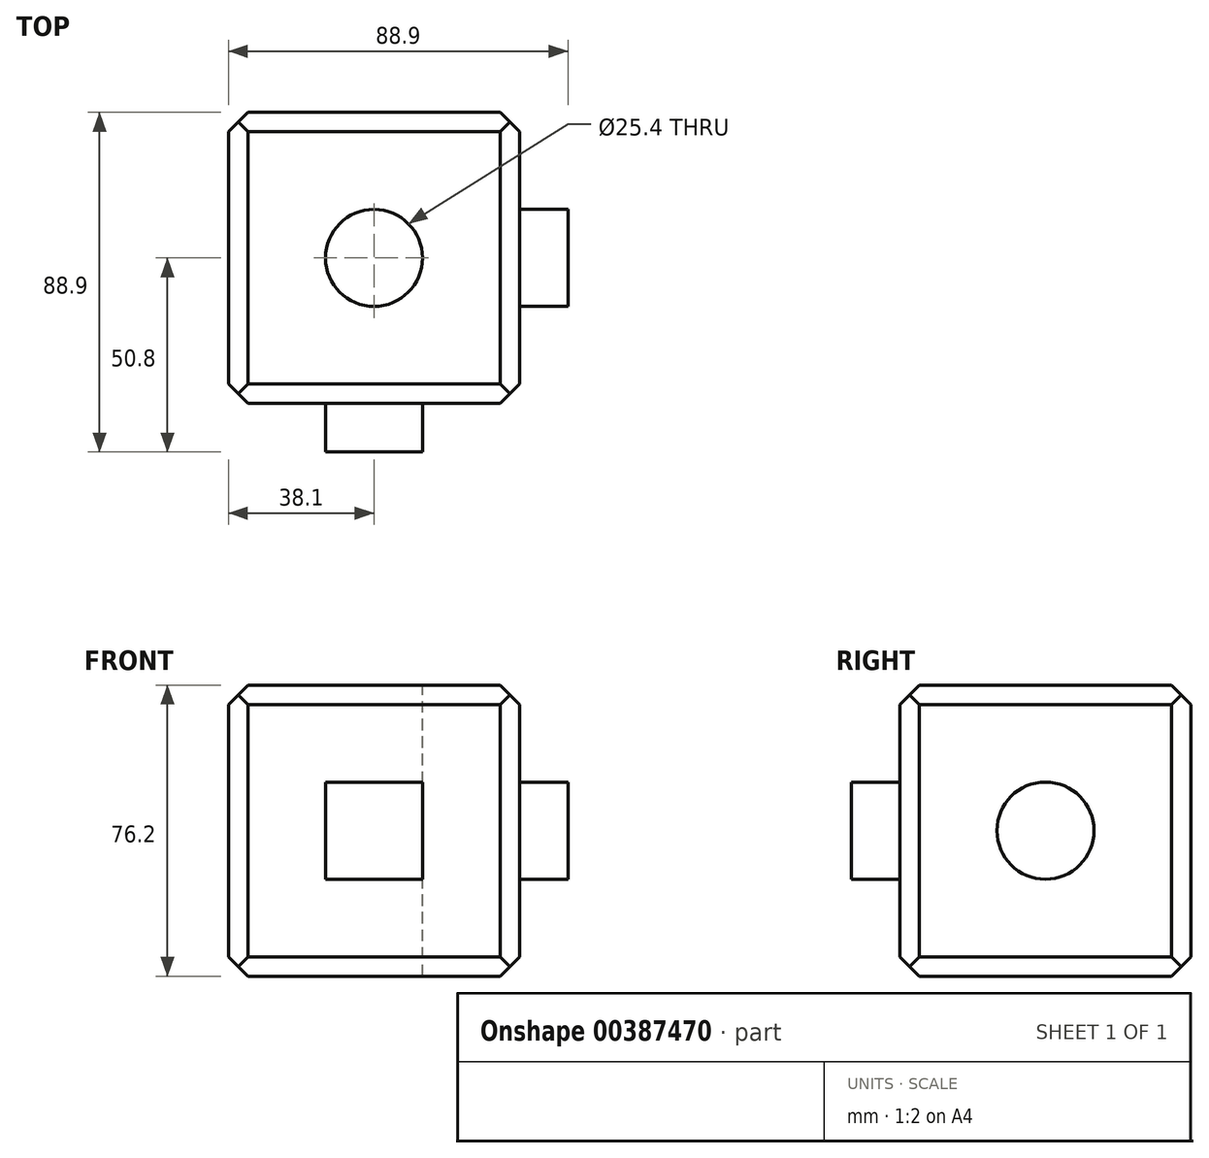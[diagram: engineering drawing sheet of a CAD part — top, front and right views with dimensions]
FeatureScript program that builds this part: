
annotation { "Feature Type Name" : "Feature", "Feature Type Description" : "" }
export const myFeature = defineFeature(function(context is Context, id is Id, definition is map)
    precondition{}
    {
        {
            var Q0;
            Q0=qCreatedBy(makeId("Front.planeOp"),FACE);
            var sketch = newSketch(context, id + "F0", { "sketchPlane" : qUnion([Q0])});
            skLineSegment(sketch, "E0.bottom", {"start": v(0, 0) * mm, "end": v(-76.2, 0) * mm});
            skLineSegment(sketch, "E0.top", {"start": v(0, 76.2) * mm, "end": v(-76.2, 76.2) * mm});
            skLineSegment(sketch, "E0.left", {"start": v(0, 0) * mm, "end": v(0, 76.2) * mm});
            skLineSegment(sketch, "E0.right", {"start": v(-76.2, 0) * mm, "end": v(-76.2, 76.2) * mm});
            skSolve(sketch);
        }
        {
            var Q0;
            Q0=makeQuery(id+"F0.imprint","IMPRINT",FACE,{"disambiguationData":[TD([[makeQuery(id+"F0.imprint","IMPRINT",EDGE,{"derivedFrom":sQuery(id+"F0.wireOp",EDGE,"E0.bottom")}),-1.0]])]});
            extrude(context, id + "F1", {"entities" : qUnion([Q0]), "depth" : 76.2 * mm});
        }
        {
            var Q0;
            Q0=makeQuery(id+"F1.opExtrude","CAP_FACE",FACE,{"disambiguationData":[OSD([sQuery(id+"F0.wireOp",EDGE,"E0.bottom"),sQuery(id+"F0.wireOp",EDGE,"E0.top"),sQuery(id+"F0.wireOp",EDGE,"E0.left"),sQuery(id+"F0.wireOp",EDGE,"E0.right")])],"isStart":false});
            var sketch = newSketch(context, id + "F2", { "sketchPlane" : qUnion([Q0])});
            skLineSegment(sketch, "E1.bottom", {"start": v(-25.4, 25.4) * mm, "end": v(-50.8, 25.4) * mm});
            skLineSegment(sketch, "E1.top", {"start": v(-25.4, 50.8) * mm, "end": v(-50.8, 50.8) * mm});
            skLineSegment(sketch, "E1.left", {"start": v(-25.4, 25.4) * mm, "end": v(-25.4, 50.8) * mm});
            skLineSegment(sketch, "E1.right", {"start": v(-50.8, 25.4) * mm, "end": v(-50.8, 50.8) * mm});
            skPoint(sketch, "E1.middle", {"position": v(-38.1, 38.1) * mm});
            skPoint(sketch, "E1.middle.positionSnap0", {"position": v(-76.2, 38.1) * mm});
            skPoint(sketch, "E1.middle.positionSnap1", {"position": v(-38.1, 76.2) * mm});
            skPoint(sketch, "E1.centerSnap0", {"position": v(-76.2, 38.1) * mm});
            skPoint(sketch, "E1.centerSnap1", {"position": v(-38.1, 76.2) * mm});
            skSolve(sketch);
        }
        {
            var Q0;
            Q0=makeQuery(id+"F2.imprint","IMPRINT",FACE,{"disambiguationData":[TD([[makeQuery(id+"F2.imprint","IMPRINT",EDGE,{"derivedFrom":sQuery(id+"F2.wireOp",EDGE,"E1.bottom")}),-1.0]])]});
            extrude(context, id + "F3", {"entities" : qUnion([Q0]), "operationType" : NewBodyOperationType.ADD, "depth" : 12.7 * mm});
        }
        {
            var Q0;
            Q0=makeQuery(id+"F1.opExtrude","SWEPT_FACE",FACE,{"disambiguationData":[OSD([sQuery(id+"F0.wireOp",EDGE,"E0.top")])]});
            var sketch = newSketch(context, id + "F4", { "sketchPlane" : qUnion([Q0])});
            skCircle(sketch, "E2", {"center": v(-38.1, -38.1) * mm, "radius": 12.7 * mm});
            skPoint(sketch, "E2.centerSnap0", {"position": v(-76.2, -38.1) * mm});
            skPoint(sketch, "E2.centerSnap1", {"position": v(-38.1, 0) * mm});
            skSolve(sketch);
        }
        {
            var Q0;
            Q0=sQuery(id+"F4.wireOp",VERTEX,"E2.center");
            var Q1;
            Q1=makeQuery(id+"F1.opExtrude","SWEPT_BODY",BODY,{"disambiguationData":[OSD([sQuery(id+"F0.wireOp",EDGE,"E0.bottom"),sQuery(id+"F0.wireOp",EDGE,"E0.top"),sQuery(id+"F0.wireOp",EDGE,"E0.left"),sQuery(id+"F0.wireOp",EDGE,"E0.right")])]});
            hole(context, id + "F5", {"style" : HoleStyle.SIMPLE, "endStyle" : HoleEndStyle.THROUGH, "holeDiameter" : 25.4 * mm, "isTappedThrough" : true, "tappedDepth" : 12.7 * mm, "tapClearance" : 3, "locations" : qUnion([Q0]), "scope" : qUnion([Q1])});
        }
        {
            var Q0;
            Q0=makeQuery(id+"F1.opExtrude","SWEPT_FACE",FACE,{"disambiguationData":[OSD([sQuery(id+"F0.wireOp",EDGE,"E0.left")])]});
            var sketch = newSketch(context, id + "F6", { "sketchPlane" : qUnion([Q0])});
            skCircle(sketch, "E3", {"center": v(-38.1, 38.1) * mm, "radius": 12.7 * mm});
            skPoint(sketch, "E3.centerSnap0", {"position": v(-76.2, 38.1) * mm});
            skPoint(sketch, "E3.centerSnap1", {"position": v(-38.1, 76.2) * mm});
            skSolve(sketch);
        }
        {
            var Q0;
            Q0=makeQuery(id+"F6.imprint","IMPRINT",FACE,{"disambiguationData":[TD([[makeQuery(id+"F6.imprint","IMPRINT",EDGE,{"derivedFrom":sQuery(id+"F6.wireOp",EDGE,"E3")}),1.0]])]});
            extrude(context, id + "F7", {"entities" : qUnion([Q0]), "operationType" : NewBodyOperationType.ADD, "depth" : 12.7 * mm});
        }
        {
            var Q0;
            Q0=makeQuery(id+"F1.opExtrude","CAP_EDGE",EDGE,{"disambiguationData":[OSD([sQuery(id+"F0.wireOp",EDGE,"E0.top")])],"isStart":false});
            var Q1;
            Q1=makeQuery(id+"F1.opExtrude","SWEPT_EDGE",EDGE,{"disambiguationData":[OSD([sQuery(id+"F0.wireOp",EDGE,"E0.top"),sQuery(id+"F0.wireOp",EDGE,"E0.left")])]});
            chamfer(context, id + "F8", {"entities" : qUnion([Q0, Q1]), "width" : 5.08 * mm, "tangentPropagation" : true});
        }
        {
            var Q0;
            Q0=makeQuery(id+"F1.opExtrude","CAP_EDGE",EDGE,{"disambiguationData":[OSD([sQuery(id+"F0.wireOp",EDGE,"E0.top")])],"isStart":true});
            chamfer(context, id + "F9", {"entities" : qUnion([Q0]), "width" : 5.08 * mm, "tangentPropagation" : true});
        }
        {
            var Q0;
            Q0=makeQuery(id+"F1.opExtrude","SWEPT_EDGE",EDGE,{"disambiguationData":[OSD([sQuery(id+"F0.wireOp",EDGE,"E0.top"),sQuery(id+"F0.wireOp",EDGE,"E0.right")])]});
            chamfer(context, id + "F10", {"entities" : qUnion([Q0]), "width" : 5.08 * mm, "tangentPropagation" : true});
        }
        {
            var Q0;
            Q0=makeQuery(id+"F1.opExtrude","CAP_EDGE",EDGE,{"disambiguationData":[OSD([sQuery(id+"F0.wireOp",EDGE,"E0.left")])],"isStart":false});
            var Q1;
            Q1=makeQuery(id+"F1.opExtrude","CAP_EDGE",EDGE,{"disambiguationData":[OSD([sQuery(id+"F0.wireOp",EDGE,"E0.right")])],"isStart":false});
            chamfer(context, id + "F11", {"entities" : qUnion([Q0, Q1]), "width" : 5.08 * mm, "tangentPropagation" : true});
        }
        {
            var Q0;
            Q0=makeQuery(id+"F1.opExtrude","CAP_EDGE",EDGE,{"disambiguationData":[OSD([sQuery(id+"F0.wireOp",EDGE,"E0.bottom")])],"isStart":false});
            chamfer(context, id + "F12", {"entities" : qUnion([Q0]), "width" : 5.08 * mm, "tangentPropagation" : true});
        }
        {
            var Q0;
            Q0=makeQuery(id+"F1.opExtrude","SWEPT_EDGE",EDGE,{"disambiguationData":[OSD([sQuery(id+"F0.wireOp",EDGE,"E0.bottom"),sQuery(id+"F0.wireOp",EDGE,"E0.left")])]});
            chamfer(context, id + "F13", {"entities" : qUnion([Q0]), "width" : 5.08 * mm, "tangentPropagation" : true});
        }
        {
            var Q0;
            Q0=makeQuery(id+"F1.opExtrude","CAP_EDGE",EDGE,{"disambiguationData":[OSD([sQuery(id+"F0.wireOp",EDGE,"E0.left")])],"isStart":true});
            chamfer(context, id + "F14", {"entities" : qUnion([Q0]), "width" : 5.08 * mm, "tangentPropagation" : true});
        }
        {
            var Q0;
            Q0=makeQuery(id+"F1.opExtrude","CAP_EDGE",EDGE,{"disambiguationData":[OSD([sQuery(id+"F0.wireOp",EDGE,"E0.right")])],"isStart":true});
            chamfer(context, id + "F15", {"entities" : qUnion([Q0]), "width" : 5.08 * mm, "tangentPropagation" : true});
        }
        {
            var Q0;
            Q0=makeQuery(id+"F1.opExtrude","SWEPT_EDGE",EDGE,{"disambiguationData":[OSD([sQuery(id+"F0.wireOp",EDGE,"E0.bottom"),sQuery(id+"F0.wireOp",EDGE,"E0.right")])]});
            chamfer(context, id + "F16", {"entities" : qUnion([Q0]), "width" : 5.08 * mm, "tangentPropagation" : true});
        }
        {
            var Q0;
            Q0=makeQuery(id+"F1.opExtrude","CAP_EDGE",EDGE,{"disambiguationData":[OSD([sQuery(id+"F0.wireOp",EDGE,"E0.bottom")])],"isStart":true});
            chamfer(context, id + "F17", {"entities" : qUnion([Q0]), "width" : 5.08 * mm, "tangentPropagation" : true});
        }
        {
            var Q0;
            Q0=makeQuery(id+"F1.opExtrude","CAP_FACE",FACE,{"disambiguationData":[OSD([sQuery(id+"F0.wireOp",EDGE,"E0.bottom"),sQuery(id+"F0.wireOp",EDGE,"E0.top"),sQuery(id+"F0.wireOp",EDGE,"E0.left"),sQuery(id+"F0.wireOp",EDGE,"E0.right")])],"isStart":false});
            var sketch = newSketch(context, id + "F18", { "sketchPlane" : qUnion([Q0])});
            skText(sketch, "E4", { "text": "Veronica", "fontName": "OpenSans-Bold.ttf"});
            const initialGuessF18  = {"E4": [-0.07383, 0.05412, 1, 0, 0.01213]};
            skSetInitialGuess(sketch, initialGuessF18);
            skSolve(sketch);
        }
        {
            var Q0;
            Q0 = qSketchRegion(id + "F18", true);
            var Q1;
            Q1 = qConstructionFilter(qBodyType(qCreatedBy(id + "F18" ,EDGE), BodyType.WIRE), ConstructionObject.NO);
            extrude(context, id + "F19", {"entities" : qUnion([Q0]), "bodyType" : ToolBodyType.SURFACE, "operationType" : NewBodyOperationType.ADD, "surfaceEntities" : qUnion([Q1]), "depth" : 17.53 * mm});
        }
    });
